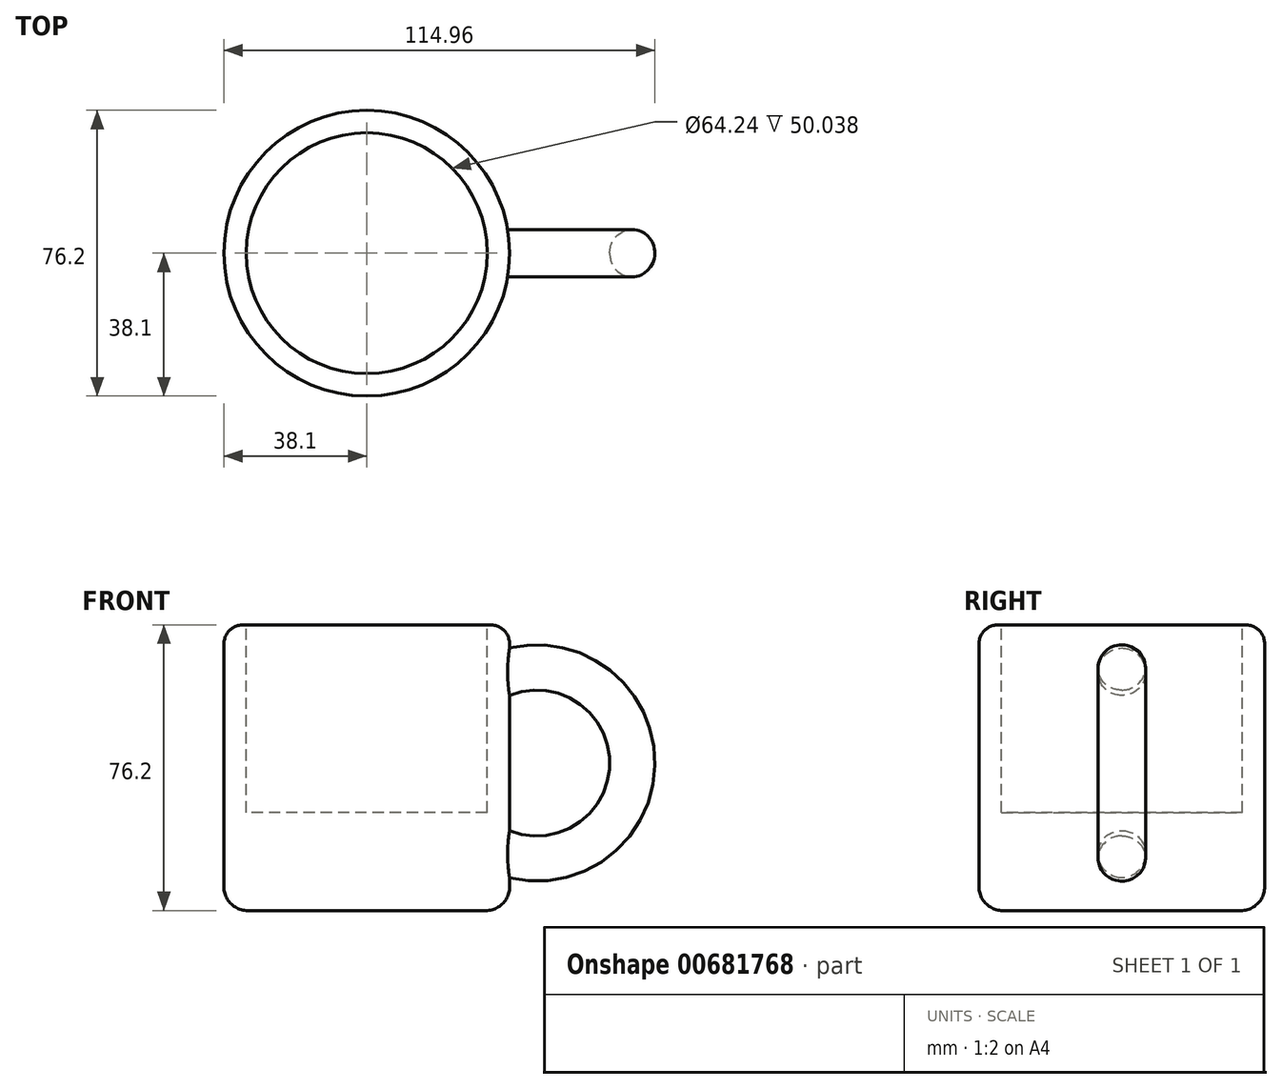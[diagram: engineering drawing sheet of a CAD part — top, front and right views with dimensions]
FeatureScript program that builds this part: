
annotation { "Feature Type Name" : "Feature", "Feature Type Description" : "" }
export const myFeature = defineFeature(function(context is Context, id is Id, definition is map)
    precondition{}
    {
        {
            var Q0;
            Q0=qCreatedBy(makeId("Top.planeOp"),FACE);
            var sketch = newSketch(context, id + "F0", { "sketchPlane" : qUnion([Q0])});
            skCircle(sketch, "E0", {"center": v(0, 0) * mm, "radius": 38.1 * mm});
            skSolve(sketch);
        }
        {
            var Q0;
            Q0=makeQuery(id+"F0.imprint","IMPRINT",FACE,{"disambiguationData":[TD([[makeQuery(id+"F0.imprint","IMPRINT",EDGE,{"derivedFrom":sQuery(id+"F0.wireOp",EDGE,"E0")}),1.0]])]});
            extrude(context, id + "F1", {"entities" : qUnion([Q0]), "depth" : 76.2 * mm, "offsetDistance" : 25.4 * mm});
        }
        {
            var Q0;
            Q0=qCreatedBy(makeId("Front.planeOp"),FACE);
            var sketch = newSketch(context, id + "F2", { "sketchPlane" : qUnion([Q0])});
            skArc(sketch, "E1", {"start": v(33.52, 16.88) * mm, "mid": v(70.76, 39.76) * mm, "end": v(32.81, 61.44) * mm});
            skSolve(sketch);
        }
        {
            var Q0;
            Q0=qCreatedBy(makeId("Right.planeOp"),FACE);
            cPlane(context, id + "F3", {"entities" : qUnion([Q0]), "cplaneType" : CPlaneType.OFFSET, "offset" : 37.85 * mm, "width" : 152.4 * mm, "height" : 152.4 * mm});
        }
        {
            var Q0;
            Q0=qCreatedBy(id+"F3.planeOp",FACE);
            var sketch = newSketch(context, id + "F4", { "sketchPlane" : qUnion([Q0])});
            skCircle(sketch, "E2", {"center": v(0, 63.62) * mm, "radius": 6.32 * mm});
            skCircle(sketch, "E3", {"center": v(0, 63.62) * mm, "radius": 6.4 * mm});
            skSolve(sketch);
        }
        {
            var Q0;
            Q0=makeQuery(id+"F4.imprint","IMPRINT",FACE,{"disambiguationData":[TD([[makeQuery(id+"F4.imprint","IMPRINT",EDGE,{"derivedFrom":sQuery(id+"F4.wireOp",EDGE,"E2")}),1.0]])]});
            var Q1;
            Q1=sQuery(id+"F2.wireOp",EDGE,"E1");
            sweep(context, id + "F5", {"operationType" : NewBodyOperationType.ADD, "profiles" : qUnion([Q0]), "path" : qUnion([Q1])});
        }
        {
            var Q0;
            Q0=makeQuery(id+"F1.opExtrude","CAP_FACE",FACE,{"disambiguationData":[OSD([sQuery(id+"F0.wireOp",EDGE,"E0")])],"isStart":false});
            var sketch = newSketch(context, id + "F6", { "sketchPlane" : qUnion([Q0])});
            skCircle(sketch, "E4", {"center": v(0, 0) * mm, "radius": 32.12 * mm});
            skSolve(sketch);
        }
        {
            var Q0;
            Q0=makeQuery(id+"F6.imprint","IMPRINT",FACE,{"disambiguationData":[TD([[makeQuery(id+"F6.imprint","IMPRINT",EDGE,{"derivedFrom":sQuery(id+"F6.wireOp",EDGE,"E4")}),1.0]])]});
            extrude(context, id + "F7", {"entities" : qUnion([Q0]), "operationType" : NewBodyOperationType.REMOVE, "oppositeDirection" : true, "depth" : 50.04 * mm, "offsetDistance" : 25.4 * mm});
        }
        {
            var Q0;
            Q0=makeQuery(id+"F1.opExtrude","CAP_EDGE",EDGE,{"disambiguationData":[OSD([sQuery(id+"F0.wireOp",EDGE,"E0")])],"isStart":false});
            fillet(context, id + "F8", {"entities" : qUnion([Q0]), "radius" : 5.08 * mm, "tangentPropagation" : true, "allowEdgeOverflow" : false});
        }
        {
            var Q0;
            Q0=makeQuery(id+"F1.opExtrude","CAP_EDGE",EDGE,{"disambiguationData":[OSD([sQuery(id+"F0.wireOp",EDGE,"E0")])],"isStart":true});
            fillet(context, id + "F9", {"entities" : qUnion([Q0]), "radius" : 6.35 * mm, "tangentPropagation" : true, "allowEdgeOverflow" : false});
        }
    });
